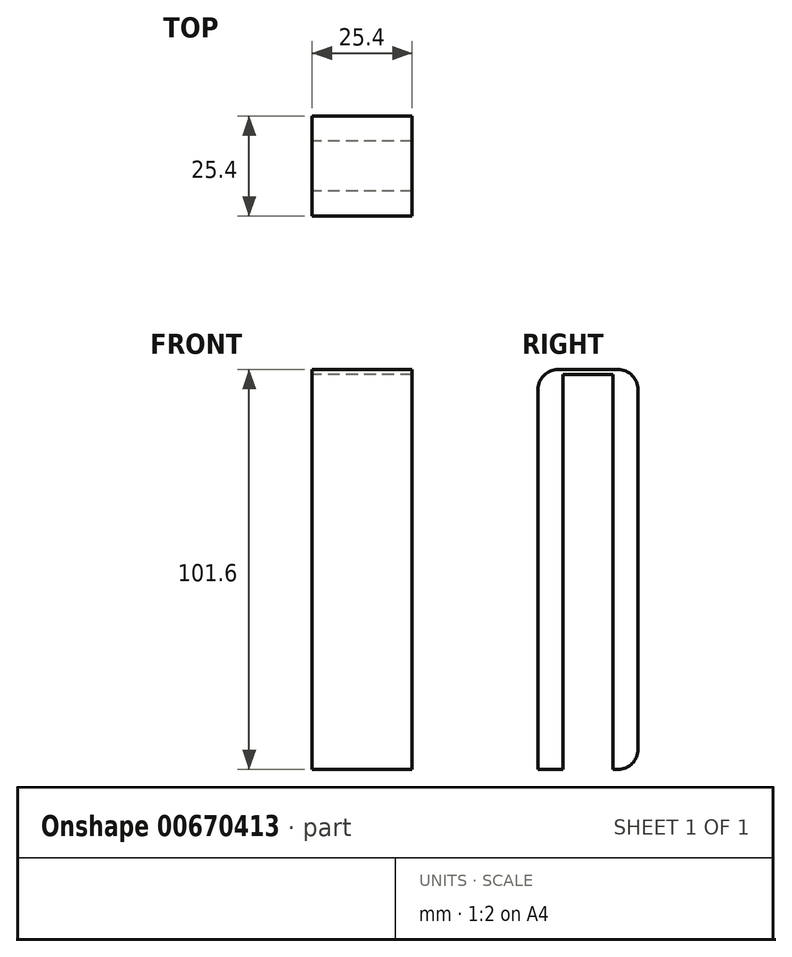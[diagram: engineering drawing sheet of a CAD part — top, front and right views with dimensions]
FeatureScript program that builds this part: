
annotation { "Feature Type Name" : "Feature", "Feature Type Description" : "" }
export const myFeature = defineFeature(function(context is Context, id is Id, definition is map)
    precondition{}
    {
        {
            var Q0;
            Q0=qCreatedBy(makeId("Right.planeOp"),FACE);
            var sketch = newSketch(context, id + "F0", { "sketchPlane" : qUnion([Q0])});
            skPoint(sketch, "E0.middle", {"position": v(0, 0) * mm});
            skLineSegment(sketch, "E1.bottom", {"start": v(22.23, -50.8) * mm, "end": v(15.88, -50.8) * mm});
            skLineSegment(sketch, "E1.top", {"start": v(22.23, 50.8) * mm, "end": v(15.88, 50.8) * mm});
            skLineSegment(sketch, "E1.left", {"start": v(22.23, -50.8) * mm, "end": v(22.23, 50.8) * mm});
            skLineSegment(sketch, "E1.right", {"start": v(15.88, -50.8) * mm, "end": v(15.88, 50.8) * mm});
            skPoint(sketch, "E1.middle", {"position": v(19.05, 0) * mm});
            skLineSegment(sketch, "E2.bottom", {"start": v(3.18, 50.8) * mm, "end": v(15.88, 50.8) * mm});
            skLineSegment(sketch, "E2.top", {"start": v(3.17, 49.53) * mm, "end": v(15.87, 49.53) * mm});
            skLineSegment(sketch, "E2.left", {"start": v(3.18, 50.8) * mm, "end": v(3.18, 49.53) * mm});
            skLineSegment(sketch, "E2.right", {"start": v(15.88, 50.8) * mm, "end": v(15.88, 49.53) * mm});
            skLineSegment(sketch, "E3.bottom", {"start": v(3.18, -50.8) * mm, "end": v(-3.17, -50.8) * mm});
            skLineSegment(sketch, "E3.top", {"start": v(3.17, 50.8) * mm, "end": v(-3.18, 50.8) * mm});
            skLineSegment(sketch, "E3.left", {"start": v(3.18, -50.8) * mm, "end": v(3.17, 50.8) * mm});
            skLineSegment(sketch, "E3.right", {"start": v(-3.17, -50.8) * mm, "end": v(-3.18, 50.8) * mm});
            skArc(sketch, "E4", {"start": v(3.18, -57.13) * mm, "mid": v(-1.3, -55.28) * mm, "end": v(-3.15, -50.8) * mm});
            skLineSegment(sketch, "E5", {"start": v(3.18, -50.8) * mm, "end": v(3.18, -57.13) * mm});
            skSolve(sketch);
        }
        {
            var Q0;
            {var subQ0=sQuery(id+"F0.wireOp",EDGE,"E2.bottom");Q0=makeQuery(id+"F0.imprint","IMPRINT",FACE,{"disambiguationData":[TD([[makeQuery(id+"F0.imprint","IMPRINT",EDGE,{"derivedFrom":subQ0}),-1.0]])]});}
            var Q1;
            {var subQ4=sQuery(id+"F0.wireOp",EDGE,"E3.top");Q1=makeQuery(id+"F0.imprint","IMPRINT",FACE,{"disambiguationData":[TD([[makeQuery(id+"F0.imprint","IMPRINT",EDGE,{"derivedFrom":subQ4}),1.0]])]});}
            var Q2;
            Q2=makeQuery(id+"F0.imprint","IMPRINT",FACE,{"disambiguationData":[TD([[makeQuery(id+"F0.imprint","IMPRINT",EDGE,{"derivedFrom":sQuery(id+"F0.wireOp",EDGE,"E1.bottom")}),-1.0]])]});
            var Q3;
            {var subQ2=sQuery(id+"F0.wireOp",EDGE,"E4");Q3=makeQuery(id+"F0.imprint","IMPRINT",FACE,{"disambiguationData":[TD([[makeQuery(id+"F0.imprint","IMPRINT",EDGE,{"derivedFrom":subQ2}),-1.0]])]});}
            extrude(context, id + "F1", {"entities" : qUnion([Q0, Q1, Q2, Q3]), "endBound" : BoundingType.SYMMETRIC, "depth" : 25.4 * mm, "offsetDistance" : 25.4 * mm});
        }
        {
            var Q0;
            Q0=makeQuery(id+"F1.opExtrude","SWEPT_EDGE",EDGE,{"disambiguationData":[OSD([sQuery(id+"F0.wireOp",EDGE,"E1.top"),sQuery(id+"F0.wireOp",EDGE,"E1.left")])]});
            var Q1;
            Q1=makeQuery(id+"F1.opExtrude","SWEPT_EDGE",EDGE,{"disambiguationData":[OSD([sQuery(id+"F0.wireOp",EDGE,"E3.top"),sQuery(id+"F0.wireOp",EDGE,"E3.right")])]});
            var Q2;
            Q2=makeQuery(id+"F1.opExtrude","SWEPT_EDGE",EDGE,{"disambiguationData":[OSD([sQuery(id+"F0.wireOp",EDGE,"E1.bottom"),sQuery(id+"F0.wireOp",EDGE,"E1.left")])]});
            fillet(context, id + "F2", {"entities" : qUnion([Q0, Q1, Q2]), "radius" : 5.08 * mm, "tangentPropagation" : true, "allowEdgeOverflow" : false});
        }
    });
